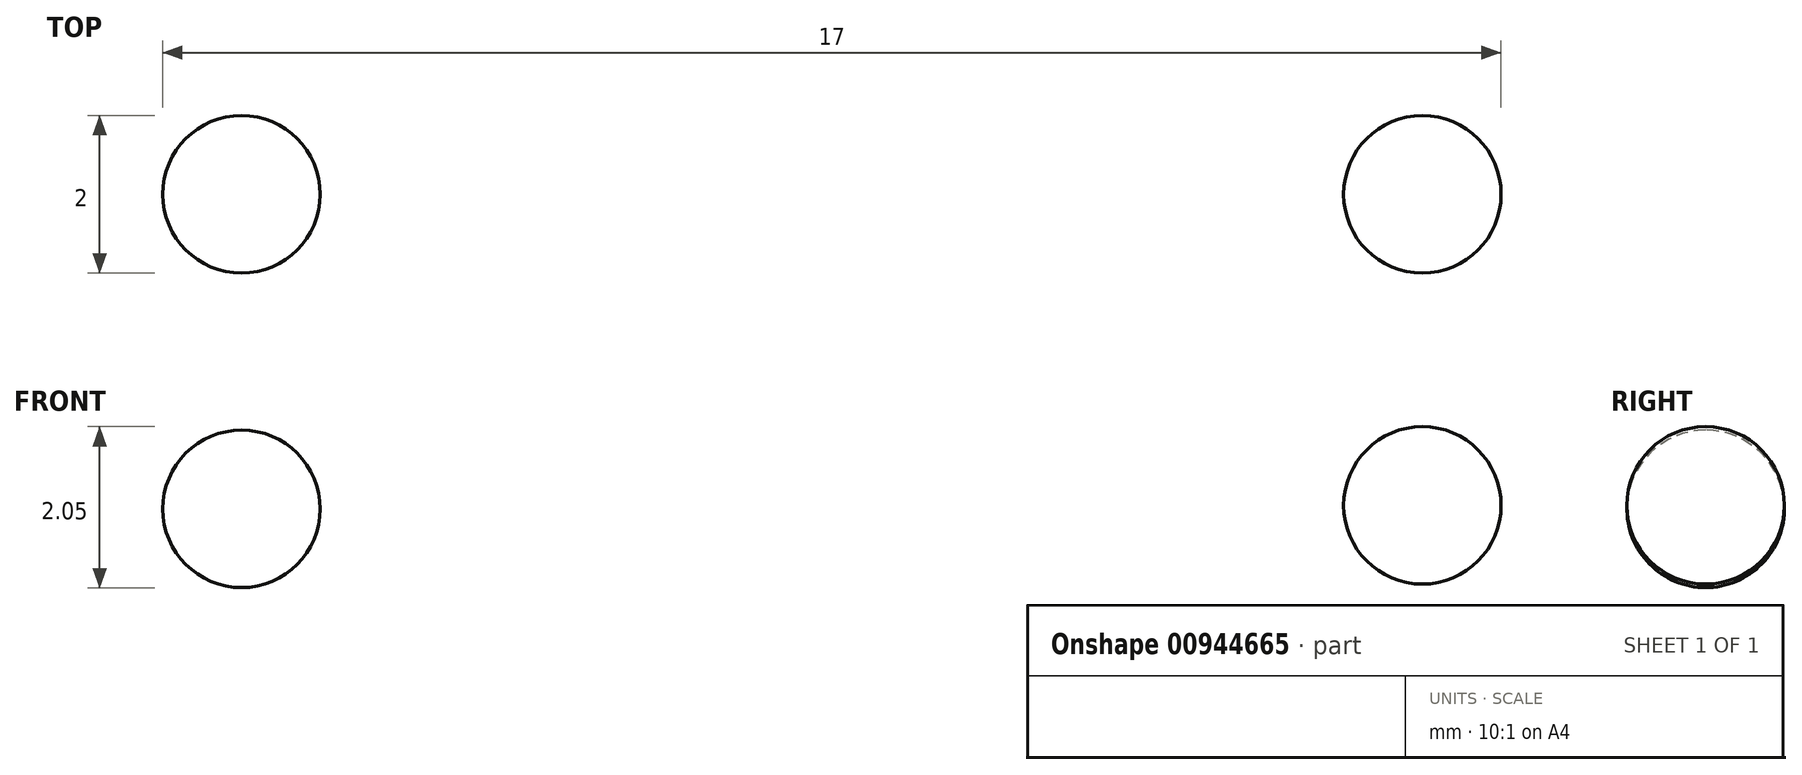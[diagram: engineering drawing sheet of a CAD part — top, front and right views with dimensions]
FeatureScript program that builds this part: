
annotation { "Feature Type Name" : "Feature", "Feature Type Description" : "" }
export const myFeature = defineFeature(function(context is Context, id is Id, definition is map)
    precondition{}
    {
        {
            var Q0;
            Q0=qCreatedBy(makeId("Front.planeOp"),FACE);
            var sketch = newSketch(context, id + "F0", { "sketchPlane" : qUnion([Q0])});
            skLineSegment(sketch, "E0", {"start": v(-30.42, 40.75) * mm, "end": v(-30.42, 38.75) * mm});
            skLineSegment(sketch, "E1", {"start": v(-15.42, 40.8) * mm, "end": v(-15.42, 38.8) * mm});
            skArc(sketch, "E2", {"start": v(-30.42, 38.75) * mm, "mid": v(-29.42, 39.75) * mm, "end": v(-30.42, 40.75) * mm});
            skArc(sketch, "E3", {"start": v(-15.42, 38.8) * mm, "mid": v(-14.42, 39.8) * mm, "end": v(-15.42, 40.8) * mm});
            skSolve(sketch);
        }
        {
            var Q0;
            Q0=makeQuery(id+"F0.imprint","IMPRINT",FACE,{"disambiguationData":[TD([[makeQuery(id+"F0.imprint","IMPRINT",EDGE,{"derivedFrom":sQuery(id+"F0.wireOp",EDGE,"E0")}),1.0]])]});
            var Q1;
            Q1=sQuery(id+"F0.wireOp",EDGE,"E0");
            revolve(context, id + "F1", {"surfaceOperationType" : NewSurfaceOperationType.NEW, "entities" : qUnion([Q0]), "axis" : qUnion([Q1]), "revolveType" : RevolveType.FULL});
        }
        {
            var Q0;
            Q0=makeQuery(id+"F0.imprint","IMPRINT",FACE,{"disambiguationData":[TD([[makeQuery(id+"F0.imprint","IMPRINT",EDGE,{"derivedFrom":sQuery(id+"F0.wireOp",EDGE,"E1")}),1.0]])]});
            var Q1;
            Q1=sQuery(id+"F0.wireOp",EDGE,"E1");
            revolve(context, id + "F2", {"surfaceOperationType" : NewSurfaceOperationType.NEW, "entities" : qUnion([Q0]), "axis" : qUnion([Q1]), "revolveType" : RevolveType.FULL});
        }
    });
